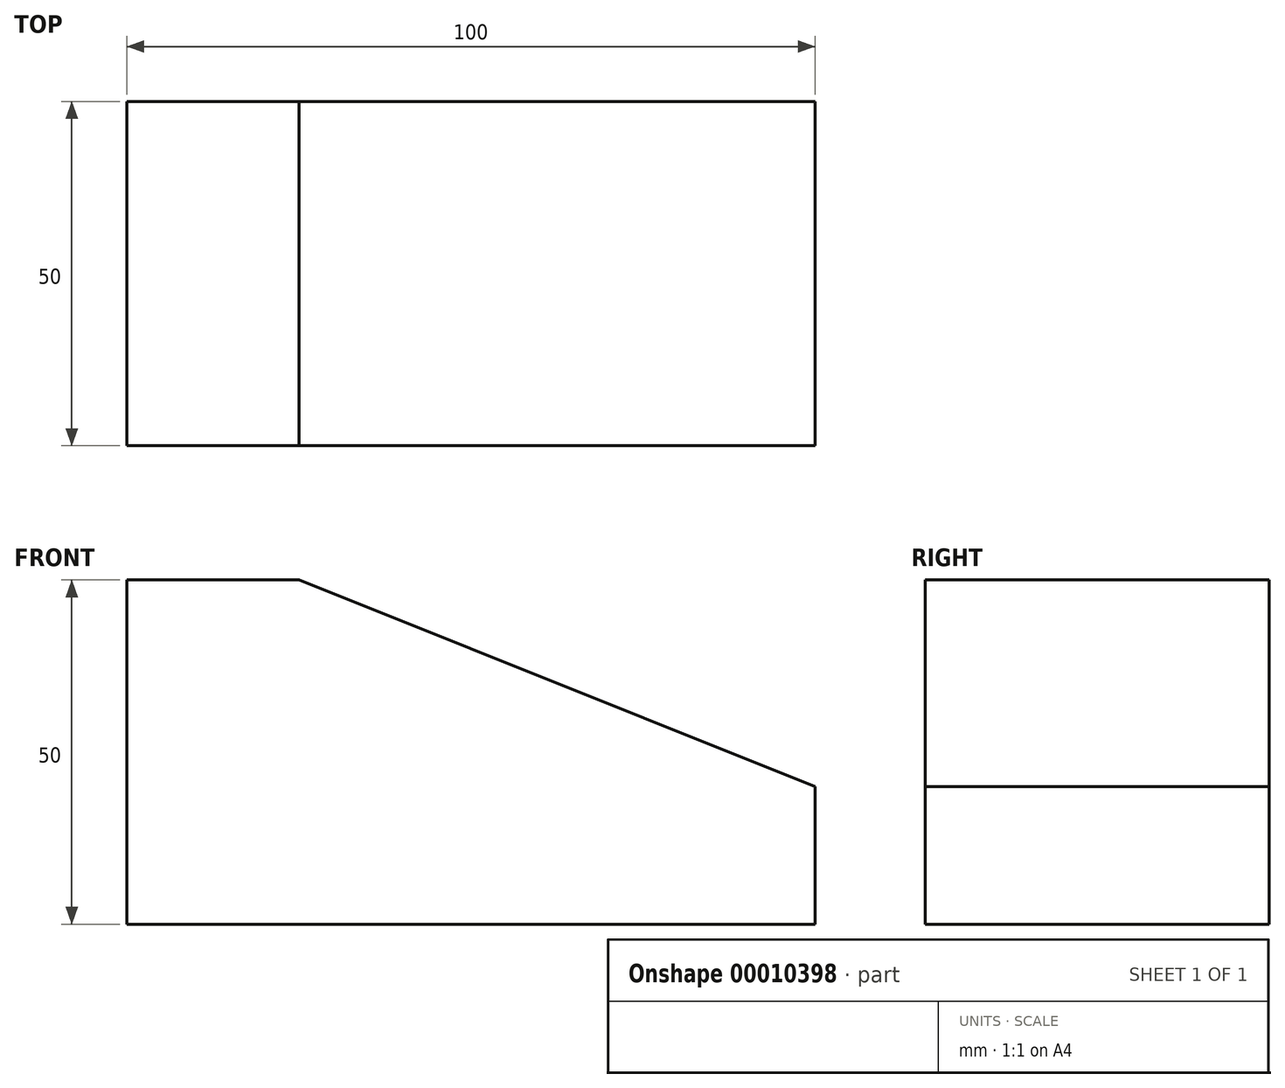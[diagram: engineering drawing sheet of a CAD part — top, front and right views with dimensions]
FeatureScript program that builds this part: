
annotation { "Feature Type Name" : "Feature", "Feature Type Description" : "" }
export const myFeature = defineFeature(function(context is Context, id is Id, definition is map)
    precondition{}
    {
        {
            var Q0;
            Q0=qCreatedBy(makeId("Front.planeOp"),FACE);
            var sketch = newSketch(context, id + "F0", { "sketchPlane" : qUnion([Q0])});
            skLineSegment(sketch, "E0", {"start": v(0, 0) * mm, "end": v(100, 0) * mm});
            skLineSegment(sketch, "E1", {"start": v(100, 0) * mm, "end": v(100, 20) * mm});
            skLineSegment(sketch, "E2", {"start": v(100, 20) * mm, "end": v(25, 50) * mm});
            skLineSegment(sketch, "E3", {"start": v(25, 50) * mm, "end": v(0, 50) * mm});
            skLineSegment(sketch, "E4", {"start": v(0, 50) * mm, "end": v(0, 0) * mm});
            skSolve(sketch);
        }
        {
            var Q0;
            Q0 = qSketchRegion(id + "F0", true);
            extrude(context, id + "F1", {"entities" : qUnion([Q0]), "oppositeDirection" : true, "depth" : 50 * mm});
        }
    });
